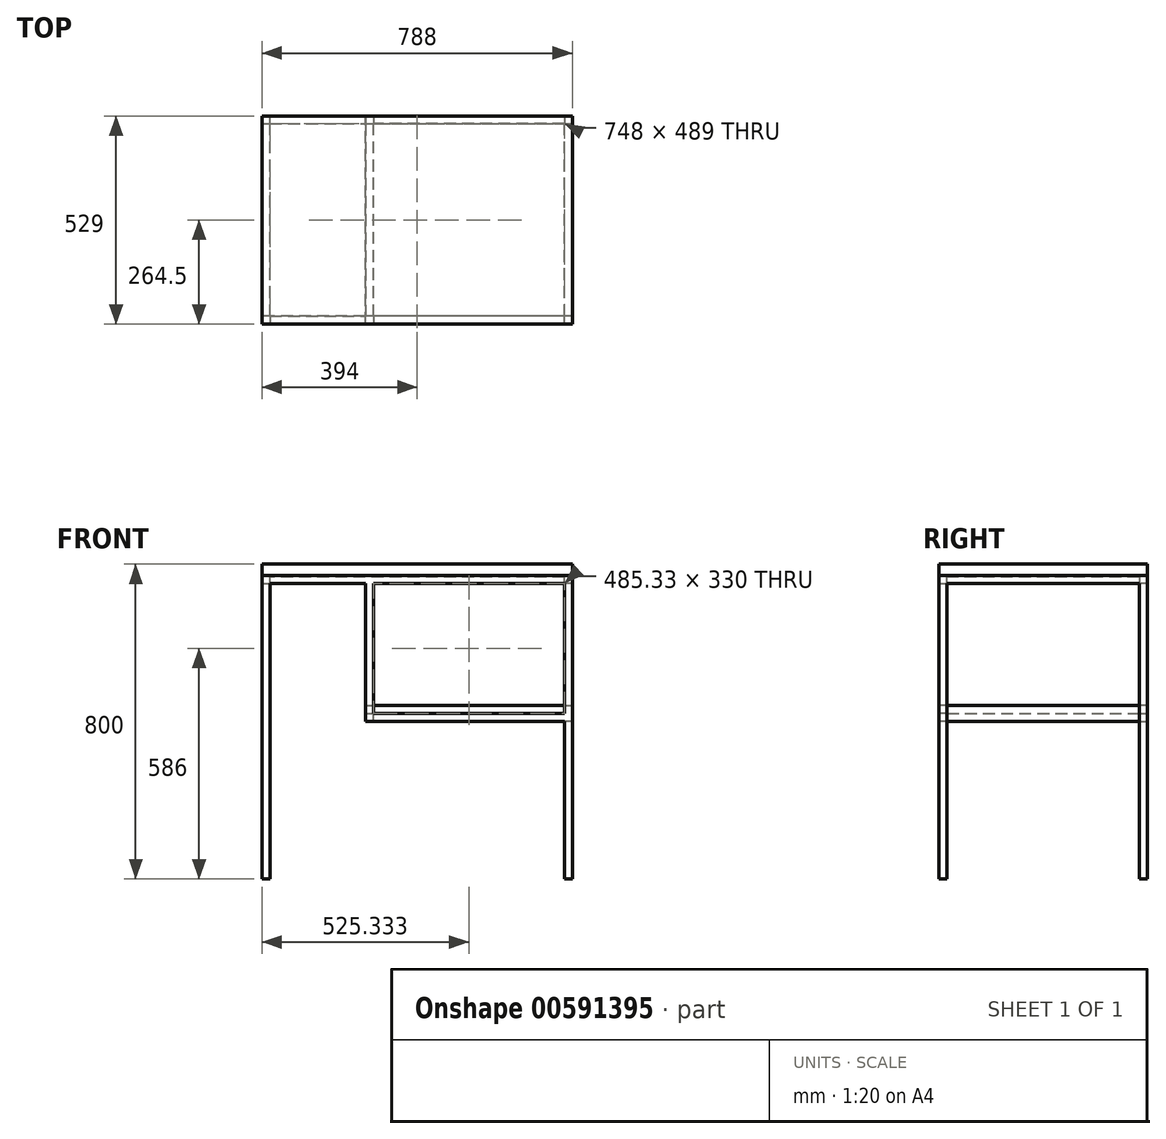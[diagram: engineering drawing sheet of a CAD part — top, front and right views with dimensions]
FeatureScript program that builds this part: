
annotation { "Feature Type Name" : "Feature", "Feature Type Description" : "" }
export const myFeature = defineFeature(function(context is Context, id is Id, definition is map)
    precondition{}
    {
        {
            assignVariable(context, id + "F0", {"name" : "epaisseur_top", "anyValue" : 33});
        }
        {
            assignVariable(context, id + "F1", {"name" : "profondeur", "anyValue" : 529});
        }
        {
            assignVariable(context, id + "F2", {"name" : "hauteur", "anyValue" : 800});
        }
        {
            assignVariable(context, id + "F3", {"name" : "enfoncement_top", "anyValue" : 4});
        }
        {
            var Q0;
            Q0=qCreatedBy(makeId("Top.planeOp"),FACE);
            var sketch = newSketch(context, id + "F4", { "sketchPlane" : qUnion([Q0])});
            skLineSegment(sketch, "E0.bottom", {"start": v(-394, 264.5) * mm, "end": v(-374, 264.5) * mm});
            skLineSegment(sketch, "E0.top", {"start": v(-394, 244.5) * mm, "end": v(-374, 244.5) * mm});
            skLineSegment(sketch, "E0.left", {"start": v(-394, 264.5) * mm, "end": v(-394, 244.5) * mm});
            skLineSegment(sketch, "E0.right", {"start": v(-374, 264.5) * mm, "end": v(-374, 244.5) * mm});
            skLineSegment(sketch, "E1.MirrorCS", {"start": v(394, 264.5) * mm, "end": v(374, 264.5) * mm});
            skLineSegment(sketch, "E2.MirrorCS", {"start": v(394, 244.5) * mm, "end": v(374, 244.5) * mm});
            skLineSegment(sketch, "E3.MirrorCS", {"start": v(374, 264.5) * mm, "end": v(374, 244.5) * mm});
            skLineSegment(sketch, "E4.MirrorCS", {"start": v(394, 264.5) * mm, "end": v(394, 244.5) * mm});
            skLineSegment(sketch, "E5.MirrorCS", {"start": v(394, -264.5) * mm, "end": v(394, -244.5) * mm});
            skLineSegment(sketch, "E6.MirrorCS", {"start": v(-394, -264.5) * mm, "end": v(-374, -264.5) * mm});
            skLineSegment(sketch, "E7.MirrorCS", {"start": v(-394, -244.5) * mm, "end": v(-374, -244.5) * mm});
            skLineSegment(sketch, "E8.MirrorCS", {"start": v(-394, -264.5) * mm, "end": v(-394, -244.5) * mm});
            skLineSegment(sketch, "E9.MirrorCS", {"start": v(-374, -264.5) * mm, "end": v(-374, -244.5) * mm});
            skLineSegment(sketch, "E10.MirrorCS", {"start": v(394, -264.5) * mm, "end": v(374, -264.5) * mm});
            skLineSegment(sketch, "E11.MirrorCS", {"start": v(394, -244.5) * mm, "end": v(374, -244.5) * mm});
            skLineSegment(sketch, "E12.MirrorCS", {"start": v(374, -264.5) * mm, "end": v(374, -244.5) * mm});
            skSolve(sketch);
        }
        {
            var Q0;
            Q0=qSketchRegion(id+"F4",true);
            extrude(context, id + "F5", {"entities" : qUnion([Q0]), "depth" : (getVariable(context, 'hauteur') - getVariable(context, 'epaisseur_top') + getVariable(context, 'enfoncement_top')) * mm});
        }
        {
            var Q0;
            Q0=makeQuery(id+"F5.opExtrude","SWEPT_FACE",FACE,{"disambiguationData":[OSD([sQuery(id+"F4.wireOp",EDGE,"E3.MirrorCS")])]});
            var sketch = newSketch(context, id + "F6", { "sketchPlane" : qUnion([Q0])});
            skLineSegment(sketch, "E13.bottom", {"start": v(-264.5, 771) * mm, "end": v(-244.5, 771) * mm});
            skLineSegment(sketch, "E13.top", {"start": v(-264.5, 751) * mm, "end": v(-244.5, 751) * mm});
            skLineSegment(sketch, "E13.left", {"start": v(-264.5, 771) * mm, "end": v(-264.5, 751) * mm});
            skLineSegment(sketch, "E13.right", {"start": v(-244.5, 771) * mm, "end": v(-244.5, 751) * mm});
            skSolve(sketch);
        }
        {
            var Q0;
            Q0=qSketchRegion(id+"F6",true);
            extrude(context, id + "F7", {"entities" : qUnion([Q0]), "endBound" : BoundingType.UP_TO_NEXT, "depth" : 25 * mm});
        }
        {
            var Q0;
            Q0=makeQuery(id+"F7.opExtrude","SWEPT_BODY",BODY,{"disambiguationData":[OSD([sQuery(id+"F6.wireOp",EDGE,"E13.bottom"),sQuery(id+"F6.wireOp",EDGE,"E13.top"),sQuery(id+"F6.wireOp",EDGE,"E13.left"),sQuery(id+"F6.wireOp",EDGE,"E13.right")])]});
            var Q1;
            Q1=qCreatedBy(makeId("Front.planeOp"),FACE);
            mirror(context, id + "F8", {"entities" : qUnion([Q0]), "mirrorPlane" : qUnion([Q1])});
        }
        {
            var Q0;
            Q0=makeQuery(id+"F5.opExtrude","SWEPT_FACE",FACE,{"disambiguationData":[OSD([sQuery(id+"F4.wireOp",EDGE,"E0.top")])]});
            var sketch = newSketch(context, id + "F9", { "sketchPlane" : qUnion([Q0])});
            skLineSegment(sketch, "E14.bottom", {"start": v(-394, 771) * mm, "end": v(-374, 771) * mm});
            skLineSegment(sketch, "E14.top", {"start": v(-394, 751) * mm, "end": v(-374, 751) * mm});
            skLineSegment(sketch, "E14.left", {"start": v(-394, 771) * mm, "end": v(-394, 751) * mm});
            skLineSegment(sketch, "E14.right", {"start": v(-374, 771) * mm, "end": v(-374, 751) * mm});
            skSolve(sketch);
        }
        {
            var Q0;
            Q0=qSketchRegion(id+"F9",true);
            extrude(context, id + "F10", {"entities" : qUnion([Q0]), "endBound" : BoundingType.UP_TO_NEXT, "depth" : 25 * mm});
        }
        {
            var Q0;
            Q0=makeQuery(id+"F10.opExtrude","SWEPT_BODY",BODY,{"disambiguationData":[OSD([sQuery(id+"F9.wireOp",EDGE,"E14.bottom"),sQuery(id+"F9.wireOp",EDGE,"E14.top"),sQuery(id+"F9.wireOp",EDGE,"E14.left"),sQuery(id+"F9.wireOp",EDGE,"E14.right")])]});
            var Q1;
            Q1=qCreatedBy(makeId("Right.planeOp"),FACE);
            mirror(context, id + "F11", {"entities" : qUnion([Q0]), "mirrorPlane" : qUnion([Q1])});
        }
        {
            var Q0;
            Q0=makeQuery(id+"F5.opExtrude","SWEPT_BODY",BODY,{"disambiguationData":[OSD([sQuery(id+"F4.wireOp",EDGE,"E0.left"),sQuery(id+"F4.wireOp",EDGE,"E0.right"),sQuery(id+"F4.wireOp",EDGE,"E0.top"),sQuery(id+"F4.wireOp",EDGE,"E0.bottom")])]});
            var Q1;
            Q1=makeQuery(id+"F11.opPattern","COPY",BODY,{"derivedFrom":makeQuery(id+"F10.opExtrude","SWEPT_BODY",BODY,{"disambiguationData":[OSD([sQuery(id+"F9.wireOp",EDGE,"E14.bottom"),sQuery(id+"F9.wireOp",EDGE,"E14.top"),sQuery(id+"F9.wireOp",EDGE,"E14.left"),sQuery(id+"F9.wireOp",EDGE,"E14.right")])]}),"instanceName":"1"});
            var Q2;
            Q2=makeQuery(id+"F5.opExtrude","SWEPT_BODY",BODY,{"disambiguationData":[OSD([sQuery(id+"F4.wireOp",EDGE,"E1.MirrorCS"),sQuery(id+"F4.wireOp",EDGE,"E3.MirrorCS"),sQuery(id+"F4.wireOp",EDGE,"E4.MirrorCS"),sQuery(id+"F4.wireOp",EDGE,"E2.MirrorCS")])]});
            var Q3;
            Q3=makeQuery(id+"F10.opExtrude","SWEPT_BODY",BODY,{"disambiguationData":[OSD([sQuery(id+"F9.wireOp",EDGE,"E14.bottom"),sQuery(id+"F9.wireOp",EDGE,"E14.top"),sQuery(id+"F9.wireOp",EDGE,"E14.left"),sQuery(id+"F9.wireOp",EDGE,"E14.right")])]});
            var Q4;
            Q4=makeQuery(id+"F5.opExtrude","SWEPT_BODY",BODY,{"disambiguationData":[OSD([sQuery(id+"F4.wireOp",EDGE,"E11.MirrorCS"),sQuery(id+"F4.wireOp",EDGE,"E5.MirrorCS"),sQuery(id+"F4.wireOp",EDGE,"E12.MirrorCS"),sQuery(id+"F4.wireOp",EDGE,"E10.MirrorCS")])]});
            var Q5;
            Q5=makeQuery(id+"F8.opPattern","COPY",BODY,{"derivedFrom":makeQuery(id+"F7.opExtrude","SWEPT_BODY",BODY,{"disambiguationData":[OSD([sQuery(id+"F6.wireOp",EDGE,"E13.bottom"),sQuery(id+"F6.wireOp",EDGE,"E13.top"),sQuery(id+"F6.wireOp",EDGE,"E13.left"),sQuery(id+"F6.wireOp",EDGE,"E13.right")])]}),"instanceName":"1"});
            var Q6;
            Q6=makeQuery(id+"F7.opExtrude","SWEPT_BODY",BODY,{"disambiguationData":[OSD([sQuery(id+"F6.wireOp",EDGE,"E13.bottom"),sQuery(id+"F6.wireOp",EDGE,"E13.top"),sQuery(id+"F6.wireOp",EDGE,"E13.left"),sQuery(id+"F6.wireOp",EDGE,"E13.right")])]});
            var Q7;
            Q7=makeQuery(id+"F5.opExtrude","SWEPT_BODY",BODY,{"disambiguationData":[OSD([sQuery(id+"F4.wireOp",EDGE,"E6.MirrorCS"),sQuery(id+"F4.wireOp",EDGE,"E7.MirrorCS"),sQuery(id+"F4.wireOp",EDGE,"E8.MirrorCS"),sQuery(id+"F4.wireOp",EDGE,"E9.MirrorCS")])]});
            booleanBodies(context, id + "F12", {"operationType" : BooleanOperationType.UNION, "tools" : qUnion([Q0, Q1, Q2, Q3, Q4, Q5, Q6, Q7])});
        }
        {
            var Q0;
            {var subQ0=makeQuery(id+"F10.opExtrude","SWEPT_FACE",FACE,{"disambiguationData":[OSD([sQuery(id+"F9.wireOp",EDGE,"E14.bottom")])]});var subQ1=makeQuery(id+"F7.opExtrude","SWEPT_FACE",FACE,{"disambiguationData":[OSD([sQuery(id+"F6.wireOp",EDGE,"E13.bottom")])]});Q0=makeQuery(id+"F12.opBoolean","MERGE",FACE,{"derivedFrom":[makeQuery(id+"F5.opExtrude","CAP_FACE",FACE,{"disambiguationData":[OSD([sQuery(id+"F4.wireOp",EDGE,"E0.left"),sQuery(id+"F4.wireOp",EDGE,"E0.right"),sQuery(id+"F4.wireOp",EDGE,"E0.top"),sQuery(id+"F4.wireOp",EDGE,"E0.bottom")])],"isStart":false}),makeQuery(id+"F5.opExtrude","CAP_FACE",FACE,{"disambiguationData":[OSD([sQuery(id+"F4.wireOp",EDGE,"E1.MirrorCS"),sQuery(id+"F4.wireOp",EDGE,"E3.MirrorCS"),sQuery(id+"F4.wireOp",EDGE,"E4.MirrorCS"),sQuery(id+"F4.wireOp",EDGE,"E2.MirrorCS")])],"isStart":false}),makeQuery(id+"F5.opExtrude","CAP_FACE",FACE,{"disambiguationData":[OSD([sQuery(id+"F4.wireOp",EDGE,"E11.MirrorCS"),sQuery(id+"F4.wireOp",EDGE,"E5.MirrorCS"),sQuery(id+"F4.wireOp",EDGE,"E12.MirrorCS"),sQuery(id+"F4.wireOp",EDGE,"E10.MirrorCS")])],"isStart":false}),makeQuery(id+"F5.opExtrude","CAP_FACE",FACE,{"disambiguationData":[OSD([sQuery(id+"F4.wireOp",EDGE,"E6.MirrorCS"),sQuery(id+"F4.wireOp",EDGE,"E7.MirrorCS"),sQuery(id+"F4.wireOp",EDGE,"E8.MirrorCS"),sQuery(id+"F4.wireOp",EDGE,"E9.MirrorCS")])],"isStart":false}),subQ1,makeQuery(id+"F8.opPattern","COPY",FACE,{"derivedFrom":subQ1,"instanceName":"1"}),subQ0,makeQuery(id+"F11.opPattern","COPY",FACE,{"derivedFrom":subQ0,"instanceName":"1"})]});}
            var sketch = newSketch(context, id + "F13", { "sketchPlane" : qUnion([Q0])});
            skLineSegment(sketch, "E15.bottom", {"start": v(-394, 264.5) * mm, "end": v(394, 264.5) * mm});
            skLineSegment(sketch, "E15.top", {"start": v(-394, -264.5) * mm, "end": v(394, -264.5) * mm});
            skLineSegment(sketch, "E15.left", {"start": v(-394, 264.5) * mm, "end": v(-394, -264.5) * mm});
            skLineSegment(sketch, "E15.right", {"start": v(394, 264.5) * mm, "end": v(394, -264.5) * mm});
            skSolve(sketch);
        }
        {
            var Q0;
            Q0=qSketchRegion(id+"F13",true);
            extrude(context, id + "F14", {"entities" : qUnion([Q0]), "depth" : (getVariable(context, 'epaisseur_top') - getVariable(context, 'enfoncement_top')) * mm, "hasSecondDirection" : true, "secondDirectionOppositeDirection" : true, "secondDirectionDepth" : (getVariable(context, 'enfoncement_top')) * mm});
        }
        {
            var Q0;
            Q0=makeQuery(id+"F5.opExtrude","SWEPT_BODY",BODY,{"disambiguationData":[OSD([sQuery(id+"F4.wireOp",EDGE,"E0.left"),sQuery(id+"F4.wireOp",EDGE,"E0.right"),sQuery(id+"F4.wireOp",EDGE,"E0.top"),sQuery(id+"F4.wireOp",EDGE,"E0.bottom")])]});
            var Q1;
            Q1=makeQuery(id+"F14.opExtrude","SWEPT_BODY",BODY,{"disambiguationData":[OSD([sQuery(id+"F13.wireOp",EDGE,"E15.bottom"),sQuery(id+"F13.wireOp",EDGE,"E15.top"),sQuery(id+"F13.wireOp",EDGE,"E15.left"),sQuery(id+"F13.wireOp",EDGE,"E15.right")])]});
            booleanBodies(context, id + "F15", {"operationType" : BooleanOperationType.SUBTRACTION, "tools" : qUnion([Q0]), "targets" : qUnion([Q1]), "keepTools" : true});
        }
        {
            var Q0;
            Q0=makeQuery(id+"F8.opPattern","COPY",FACE,{"derivedFrom":makeQuery(id+"F7.opExtrude","SWEPT_FACE",FACE,{"disambiguationData":[OSD([sQuery(id+"F6.wireOp",EDGE,"E13.top")])]}),"instanceName":"1"});
            var sketch = newSketch(context, id + "F16", { "sketchPlane" : qUnion([Q0])});
            skLineSegment(sketch, "E16.bottom", {"start": v(-131.33, 264.5) * mm, "end": v(-111.33, 264.5) * mm});
            skLineSegment(sketch, "E16.top", {"start": v(-131.33, 244.5) * mm, "end": v(-111.33, 244.5) * mm});
            skLineSegment(sketch, "E16.left", {"start": v(-131.33, 264.5) * mm, "end": v(-131.33, 244.5) * mm});
            skLineSegment(sketch, "E16.right", {"start": v(-111.33, 264.5) * mm, "end": v(-111.33, 244.5) * mm});
            skSolve(sketch);
        }
        {
            var Q0;
            Q0=qSketchRegion(id+"F16",true);
            extrude(context, id + "F17", {"entities" : qUnion([Q0]), "depth" : 350 * mm, "offsetDistance" : 25 * mm});
        }
        {
            var Q0;
            Q0=makeQuery(id+"F17.opExtrude","SWEPT_FACE",FACE,{"disambiguationData":[OSD([sQuery(id+"F16.wireOp",EDGE,"E16.right")])]});
            var sketch = newSketch(context, id + "F18", { "sketchPlane" : qUnion([Q0])});
            skLineSegment(sketch, "E17.bottom", {"start": v(-264.5, 401) * mm, "end": v(-244.5, 401) * mm});
            skLineSegment(sketch, "E17.top", {"start": v(-264.5, 421) * mm, "end": v(-244.5, 421) * mm});
            skLineSegment(sketch, "E17.left", {"start": v(-264.5, 401) * mm, "end": v(-264.5, 421) * mm});
            skLineSegment(sketch, "E17.right", {"start": v(-244.5, 401) * mm, "end": v(-244.5, 421) * mm});
            skSolve(sketch);
        }
        {
            var Q0;
            Q0=makeQuery(id+"F18.imprint","IMPRINT",FACE,{"disambiguationData":[TD([[makeQuery(id+"F18.imprint","IMPRINT",EDGE,{"derivedFrom":sQuery(id+"F18.wireOp",EDGE,"E17.bottom")}),1.0]])]});
            extrude(context, id + "F19", {"entities" : qUnion([Q0]), "endBound" : BoundingType.UP_TO_NEXT, "depth" : 25 * mm});
        }
        {
            var Q0;
            Q0=makeQuery(id+"F17.opExtrude","SWEPT_BODY",BODY,{"disambiguationData":[OSD([sQuery(id+"F16.wireOp",EDGE,"E16.bottom"),sQuery(id+"F16.wireOp",EDGE,"E16.top"),sQuery(id+"F16.wireOp",EDGE,"E16.left"),sQuery(id+"F16.wireOp",EDGE,"E16.right")])]});
            var Q1;
            Q1=makeQuery(id+"F19.opExtrude","SWEPT_BODY",BODY,{"disambiguationData":[OSD([sQuery(id+"F18.wireOp",EDGE,"E17.bottom"),sQuery(id+"F18.wireOp",EDGE,"E17.top"),sQuery(id+"F18.wireOp",EDGE,"E17.left"),sQuery(id+"F18.wireOp",EDGE,"E17.right")])]});
            var Q2;
            Q2=qCreatedBy(makeId("Front.planeOp"),FACE);
            mirror(context, id + "F20", {"operationType" : NewBodyOperationType.ADD, "entities" : qUnion([Q0, Q1]), "mirrorPlane" : qUnion([Q2])});
        }
        {
            var Q0;
            {var subQ0=makeQuery(id+"F7.opExtrude","SWEPT_FACE",FACE,{"disambiguationData":[OSD([sQuery(id+"F6.wireOp",EDGE,"E13.right")])]});var subQ1=makeQuery(id+"F5.opExtrude","SWEPT_FACE",FACE,{"disambiguationData":[OSD([sQuery(id+"F4.wireOp",EDGE,"E2.MirrorCS")])]});Q0=makeQuery(id+"F20.boolean.opBoolean","MERGE",FACE,{"derivedFrom":[makeQuery(id+"F12.opBoolean","MERGE",FACE,{"derivedFrom":[subQ1,subQ0]}),makeQuery(id+"F12.opBoolean","MERGE",FACE,{"disambiguationData":[OD(1.0)],"derivedFrom":[makeQuery(id+"F5.opExtrude","SWEPT_FACE",FACE,{"disambiguationData":[OSD([sQuery(id+"F4.wireOp",EDGE,"E0.top")])]}),subQ1,subQ0]}),makeQuery(id+"F20.opPattern","COPY",FACE,{"derivedFrom":makeQuery(id+"F17.opExtrude","SWEPT_FACE",FACE,{"disambiguationData":[OSD([sQuery(id+"F16.wireOp",EDGE,"E16.top")])]}),"instanceName":"1"}),makeQuery(id+"F20.opPattern","COPY",FACE,{"derivedFrom":makeQuery(id+"F19.opExtrude","SWEPT_FACE",FACE,{"disambiguationData":[OSD([sQuery(id+"F18.wireOp",EDGE,"E17.right")])]}),"instanceName":"1"})]});}
            var sketch = newSketch(context, id + "F21", { "sketchPlane" : qUnion([Q0])});
            skLineSegment(sketch, "E18.bottom", {"start": v(-131.33, 401) * mm, "end": v(-111.33, 401) * mm});
            skLineSegment(sketch, "E18.top", {"start": v(-131.33, 421) * mm, "end": v(-111.33, 421) * mm});
            skLineSegment(sketch, "E18.left", {"start": v(-131.33, 401) * mm, "end": v(-131.33, 421) * mm});
            skLineSegment(sketch, "E18.right", {"start": v(-111.33, 401) * mm, "end": v(-111.33, 421) * mm});
            skSolve(sketch);
        }
        {
            var Q0;
            Q0=qSketchRegion(id+"F21",true);
            extrude(context, id + "F22", {"entities" : qUnion([Q0]), "operationType" : NewBodyOperationType.ADD, "endBound" : BoundingType.UP_TO_NEXT, "depth" : 25 * mm});
        }
        {
            var Q0;
            Q0=makeQuery(id+"F20.boolean.opBoolean","MERGE",FACE,{"derivedFrom":[makeQuery(id+"F12.opBoolean","MERGE",FACE,{"derivedFrom":[makeQuery(id+"F5.opExtrude","SWEPT_FACE",FACE,{"disambiguationData":[OSD([sQuery(id+"F4.wireOp",EDGE,"E6.MirrorCS")])]}),makeQuery(id+"F5.opExtrude","SWEPT_FACE",FACE,{"disambiguationData":[OSD([sQuery(id+"F4.wireOp",EDGE,"E10.MirrorCS")])]}),makeQuery(id+"F8.opPattern","COPY",FACE,{"derivedFrom":makeQuery(id+"F7.opExtrude","SWEPT_FACE",FACE,{"disambiguationData":[OSD([sQuery(id+"F6.wireOp",EDGE,"E13.left")])]}),"instanceName":"1"})]}),makeQuery(id+"F17.opExtrude","SWEPT_FACE",FACE,{"disambiguationData":[OSD([sQuery(id+"F16.wireOp",EDGE,"E16.bottom")])]}),makeQuery(id+"F19.opExtrude","SWEPT_FACE",FACE,{"disambiguationData":[OSD([sQuery(id+"F18.wireOp",EDGE,"E17.left")])]})]});
            var sketch = newSketch(context, id + "F23", { "sketchPlane" : qUnion([Q0])});
            skLineSegment(sketch, "E19.bottom", {"start": v(-131.33, 441) * mm, "end": v(394, 441) * mm});
            skLineSegment(sketch, "E19.top", {"start": v(-131.33, 401) * mm, "end": v(394, 401) * mm});
            skLineSegment(sketch, "E19.left", {"start": v(-131.33, 441) * mm, "end": v(-131.33, 401) * mm});
            skLineSegment(sketch, "E19.right", {"start": v(394, 441) * mm, "end": v(394, 401) * mm});
            skSolve(sketch);
        }
        {
            var Q0;
            Q0=qSketchRegion(id+"F23",true);
            extrude(context, id + "F24", {"entities" : qUnion([Q0]), "oppositeDirection" : true, "depth" : (getVariable(context, 'profondeur')) * mm});
        }
        {
            var Q0;
            Q0=makeQuery(id+"F5.opExtrude","SWEPT_BODY",BODY,{"disambiguationData":[OSD([sQuery(id+"F4.wireOp",EDGE,"E0.left"),sQuery(id+"F4.wireOp",EDGE,"E0.right"),sQuery(id+"F4.wireOp",EDGE,"E0.top"),sQuery(id+"F4.wireOp",EDGE,"E0.bottom")])]});
            var Q1;
            Q1=makeQuery(id+"F24.opExtrude","SWEPT_BODY",BODY,{"disambiguationData":[OSD([sQuery(id+"F23.wireOp",EDGE,"E19.bottom"),sQuery(id+"F23.wireOp",EDGE,"E19.top"),sQuery(id+"F23.wireOp",EDGE,"E19.left"),sQuery(id+"F23.wireOp",EDGE,"E19.right")])]});
            booleanBodies(context, id + "F25", {"operationType" : BooleanOperationType.SUBTRACTION, "tools" : qUnion([Q0]), "targets" : qUnion([Q1]), "keepTools" : true});
        }
    });
